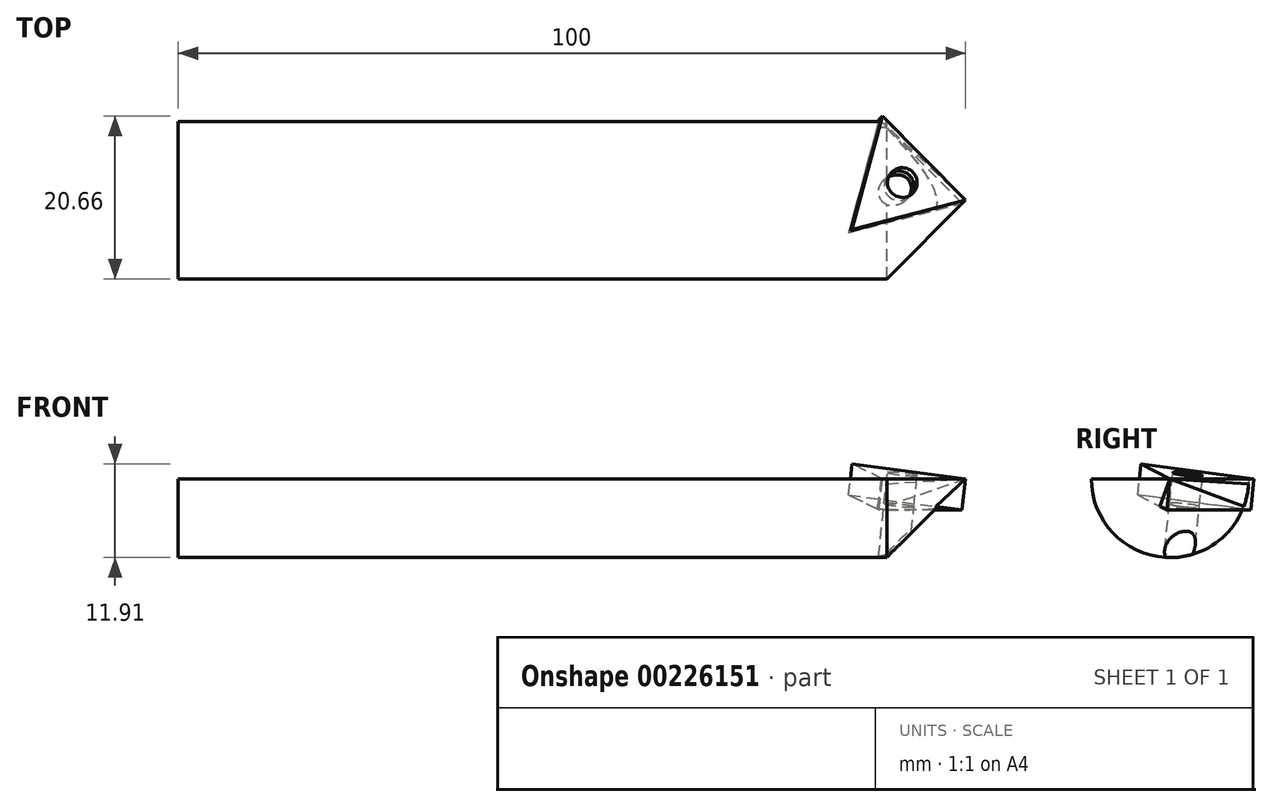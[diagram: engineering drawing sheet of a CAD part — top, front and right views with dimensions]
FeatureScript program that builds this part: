
annotation { "Feature Type Name" : "Feature", "Feature Type Description" : "" }
export const myFeature = defineFeature(function(context is Context, id is Id, definition is map)
    precondition{}
    {
        {
            var Q0;
            Q0=qCreatedBy(makeId("Top.planeOp"),FACE);
            var sketch = newSketch(context, id + "F0", { "sketchPlane" : qUnion([Q0])});
            skLineSegment(sketch, "E0", {"start": v(-113.28, 0) * mm, "end": v(15.69, 0) * mm, "construction": true});
            skLineSegment(sketch, "E1", {"start": v(0, 0) * mm, "end": v(-10, 10) * mm});
            skLineSegment(sketch, "E2", {"start": v(-10, 10) * mm, "end": v(-100, 10) * mm});
            skLineSegment(sketch, "E3", {"start": v(-100, 10) * mm, "end": v(-100, 0) * mm});
            skLineSegment(sketch, "E4", {"start": v(-100, 0) * mm, "end": v(0, 0) * mm});
            skSolve(sketch);
        }
        {
            var Q0;
            Q0 = qSketchRegion(id + "F0", true);
            var Q1;
            Q1=sQuery(id+"F0.wireOp",EDGE,"E0");
            revolve(context, id + "F1", {"entities" : qUnion([Q0]), "axis" : qUnion([Q1]), "revolveType" : RevolveType.ONE_DIRECTION, "oppositeDirection" : true, "angle" : 180 * degree});
        }
        {
            var Q0;
            Q0=qCreatedBy(makeId("Top.planeOp"),FACE);
            var sketch = newSketch(context, id + "F2", { "sketchPlane" : qUnion([Q0])});
            skLineSegment(sketch, "E5", {"start": v(0, 0) * mm, "end": v(-13, 7.5) * mm});
            skLineSegment(sketch, "E6", {"start": v(-13, 7.5) * mm, "end": v(-13, -7.5) * mm});
            skLineSegment(sketch, "E7", {"start": v(-13, -7.5) * mm, "end": v(0, 0) * mm});
            skLineSegment(sketch, "E8", {"start": v(0, -10.11) * mm, "end": v(0, 15.26) * mm, "construction": true});
            skLineSegment(sketch, "E9", {"start": v(0, 0) * mm, "end": v(-4.35, 0) * mm, "construction": true});
            skCircle(sketch, "E10", {"center": v(-8.34, 0) * mm, "radius": 1.9 * mm});
            skPoint(sketch, "E10.centerSnap0", {"position": v(-13, 0) * mm});
            skSolve(sketch);
        }
        {
            var Q0;
            Q0 = qSketchRegion(id + "F2", true);
            extrude(context, id + "F3", {"entities" : qUnion([Q0]), "oppositeDirection" : true, "depth" : 4 * mm});
        }
        {
            var Q0;
            Q0=makeQuery(id+"F3.opExtrude","SWEPT_BODY",BODY,{"disambiguationData":[OSD([sQuery(id+"F2.wireOp",EDGE,"E5"),sQuery(id+"F2.wireOp",EDGE,"E6"),sQuery(id+"F2.wireOp",EDGE,"E7")])]});
            var Q1;
            Q1=makeQuery(id+"F3.opExtrude","SWEPT_EDGE",EDGE,{"disambiguationData":[OSD([sQuery(id+"F2.wireOp",EDGE,"E5"),sQuery(id+"F2.wireOp",EDGE,"E7")])]});
            transform(context, id + "F4", {"entities" : qUnion([Q0]), "transformType" : TransformType.ROTATION, "transformAxis" : qUnion([Q1]), "angle" : 15 * degree, "oppositeDirection" : true, "makeCopy" : false});
        }
        {
            var Q0;
            Q0=makeQuery(id+"F3.opExtrude","SWEPT_BODY",BODY,{"disambiguationData":[OSD([sQuery(id+"F2.wireOp",EDGE,"E5"),sQuery(id+"F2.wireOp",EDGE,"E6"),sQuery(id+"F2.wireOp",EDGE,"E7")])]});
            var Q1;
            Q1=sQuery(id+"F2.wireOp",EDGE,"E8");
            transform(context, id + "F5", {"entities" : qUnion([Q0]), "transformType" : TransformType.ROTATION, "transformAxis" : qUnion([Q1]), "angle" : 6 * degree, "makeCopy" : false});
        }
        {
            var Q0;
            Q0=makeQuery(id+"F3.opExtrude","SWEPT_BODY",BODY,{"disambiguationData":[OSD([sQuery(id+"F2.wireOp",EDGE,"E5"),sQuery(id+"F2.wireOp",EDGE,"E6"),sQuery(id+"F2.wireOp",EDGE,"E7")])]});
            var Q1;
            Q1=sQuery(id+"F2.wireOp",EDGE,"E9");
            transform(context, id + "F6", {"entities" : qUnion([Q0]), "transformType" : TransformType.ROTATION, "transformAxis" : qUnion([Q1]), "angle" : 6 * degree, "makeCopy" : false});
        }
        {
            var Q0;
            Q0=makeQuery(id+"F3.opExtrude","SWEPT_BODY",BODY,{"disambiguationData":[OSD([sQuery(id+"F2.wireOp",EDGE,"E5"),sQuery(id+"F2.wireOp",EDGE,"E6"),sQuery(id+"F2.wireOp",EDGE,"E7")])]});
            var Q1;
            Q1=makeQuery(id+"F1.opRevolve","SWEPT_BODY",BODY,{"disambiguationData":[OSD([sQuery(id+"F0.wireOp",EDGE,"E1"),sQuery(id+"F0.wireOp",EDGE,"E2"),sQuery(id+"F0.wireOp",EDGE,"E3"),sQuery(id+"F0.wireOp",EDGE,"E4")])]});
            booleanBodies(context, id + "F7", {"operationType" : BooleanOperationType.SUBTRACTION, "tools" : qUnion([Q0]), "targets" : qUnion([Q1]), "keepTools" : true});
        }
        {
            var Q0;
            Q0=makeQuery(id+"F7.opBoolean","COPY",FACE,{"derivedFrom":makeQuery(id+"F3.opExtrude","CAP_FACE",FACE,{"disambiguationData":[OSD([sQuery(id+"F2.wireOp",EDGE,"E5"),sQuery(id+"F2.wireOp",EDGE,"E6"),sQuery(id+"F2.wireOp",EDGE,"E7"),sQuery(id+"F2.wireOp",EDGE,"E10")])],"isStart":false})});
            var sketch = newSketch(context, id + "F8", { "sketchPlane" : qUnion([Q0])});
            skCircle(sketch, "E11.0", {"center": v(-8.06, 2.16) * mm, "radius": 1.9 * mm});
            skSolve(sketch);
        }
        {
            var Q0;
            Q0 = qSketchRegion(id + "F8", true);
            extrude(context, id + "F9", {"entities" : qUnion([Q0]), "operationType" : NewBodyOperationType.REMOVE, "oppositeDirection" : true, "depth" : 25 * mm, "symmetric" : true});
        }
    });
